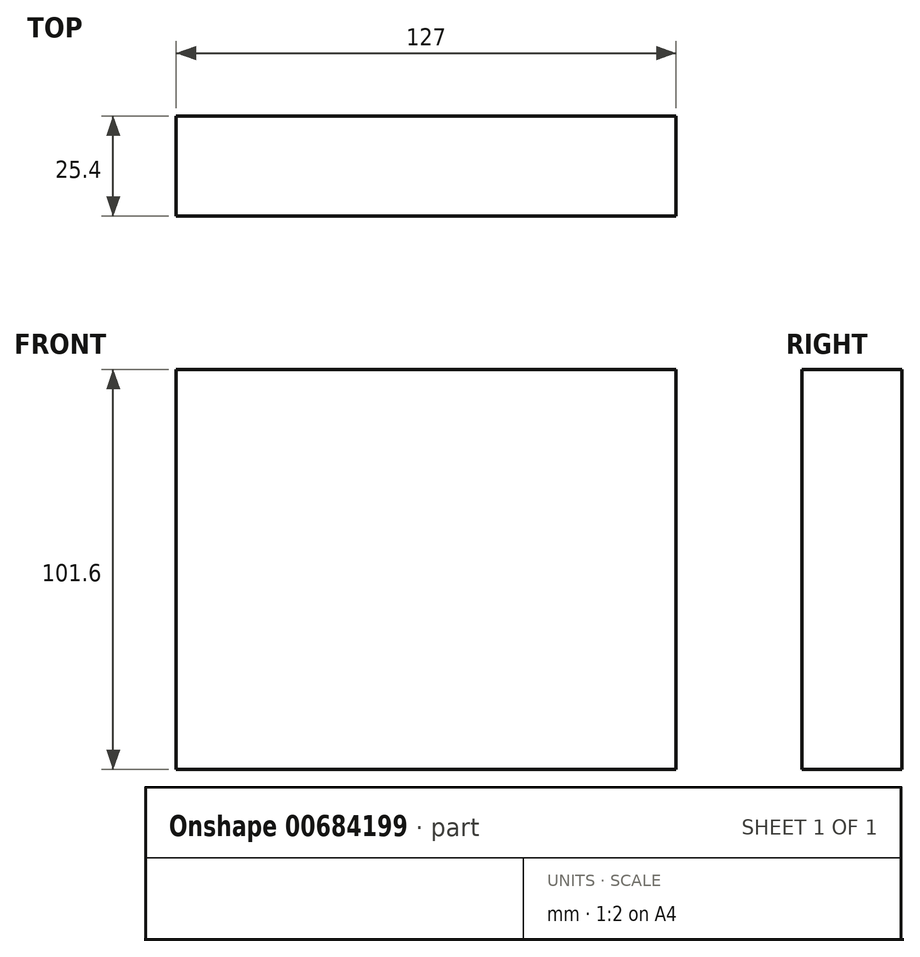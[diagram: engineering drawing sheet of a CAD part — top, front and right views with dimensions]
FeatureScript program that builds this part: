
annotation { "Feature Type Name" : "Feature", "Feature Type Description" : "" }
export const myFeature = defineFeature(function(context is Context, id is Id, definition is map)
    precondition{}
    {
        {
            var Q0;
            Q0=qCreatedBy(makeId("Front.planeOp"),FACE);
            var sketch = newSketch(context, id + "F0", { "sketchPlane" : qUnion([Q0])});
            skLineSegment(sketch, "E0.bottom", {"start": v(-61.82, 54.6) * mm, "end": v(65.18, 54.6) * mm});
            skLineSegment(sketch, "E0.top", {"start": v(-61.82, -47) * mm, "end": v(65.18, -47) * mm});
            skLineSegment(sketch, "E0.left", {"start": v(-61.82, 54.6) * mm, "end": v(-61.82, -47) * mm});
            skLineSegment(sketch, "E0.right", {"start": v(65.18, 54.6) * mm, "end": v(65.18, -47) * mm});
            skSolve(sketch);
        }
        {
            var Q0;
            Q0 = qSketchRegion(id + "F0", true);
            extrude(context, id + "F1", {"entities" : qUnion([Q0]), "depth" : 25.4 * mm, "offsetDistance" : 25.4 * mm});
        }
    });
